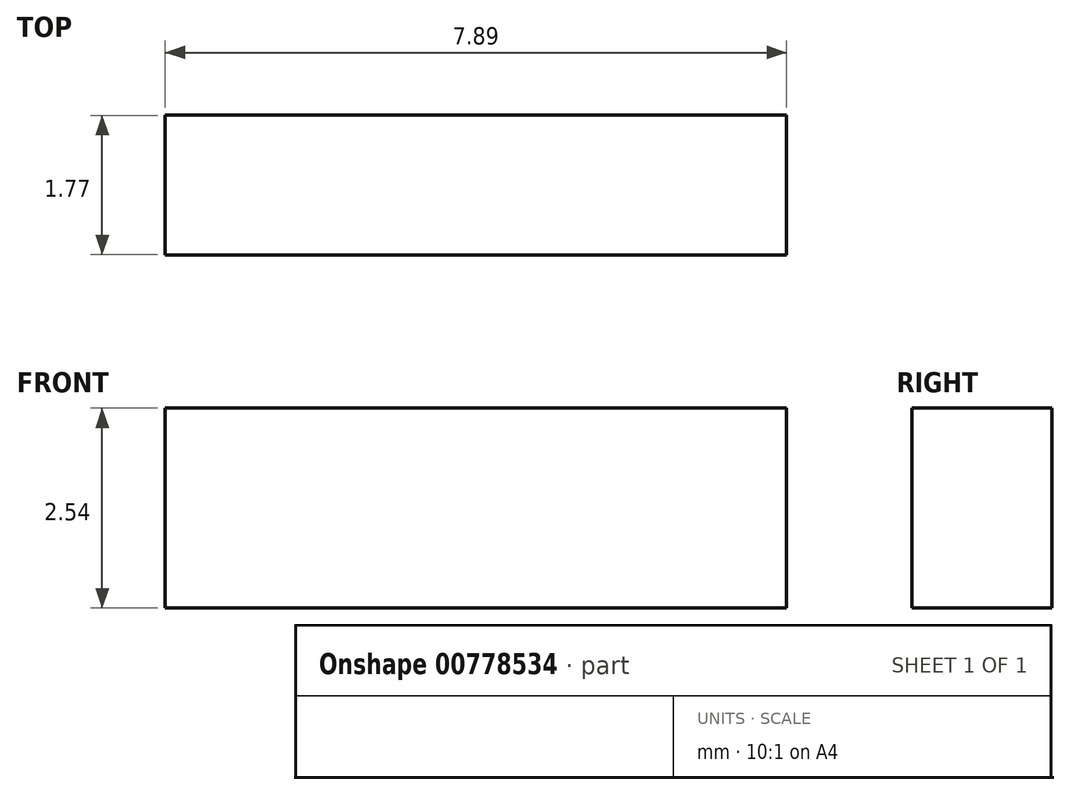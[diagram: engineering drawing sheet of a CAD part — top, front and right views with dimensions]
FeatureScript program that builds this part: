
annotation { "Feature Type Name" : "Feature", "Feature Type Description" : "" }
export const myFeature = defineFeature(function(context is Context, id is Id, definition is map)
    precondition{}
    {
        {
            var Q0;
            Q0=qCreatedBy(makeId("Front.planeOp"),FACE);
            var sketch = newSketch(context, id + "F0", { "sketchPlane" : qUnion([Q0])});
            skLineSegment(sketch, "E0.bottom", {"start": v(-12.97, 25.4) * mm, "end": v(11.1, 25.4) * mm});
            skLineSegment(sketch, "E0.top", {"start": v(-12.97, -20.32) * mm, "end": v(11.1, -20.32) * mm});
            skLineSegment(sketch, "E0.left", {"start": v(-12.97, 25.4) * mm, "end": v(-12.97, -20.32) * mm});
            skLineSegment(sketch, "E0.right", {"start": v(11.1, 25.4) * mm, "end": v(11.1, -20.32) * mm});
            skLineSegment(sketch, "E1", {"start": v(0, 9.9) * mm, "end": v(0, 4.81) * mm});
            skLineSegment(sketch, "E2", {"start": v(0, 4.81) * mm, "end": v(7.89, 4.81) * mm});
            skLineSegment(sketch, "E3", {"start": v(7.89, 4.81) * mm, "end": v(7.89, 9.9) * mm});
            skLineSegment(sketch, "E4", {"start": v(7.89, 9.9) * mm, "end": v(0, 9.9) * mm});
            skLineSegment(sketch, "E5", {"start": v(0, 7.35) * mm, "end": v(7.89, 7.35) * mm});
            skSolve(sketch);
        }
        {
            var Q0;
            Q0=makeQuery(id+"F0.imprint","IMPRINT",FACE,{"disambiguationData":[TD([[makeQuery(id+"F0.imprint","IMPRINT",EDGE,{"derivedFrom":sQuery(id+"F0.wireOp",EDGE,"E0.bottom")}),-1.0]])]});
            extrude(context, id + "F1", {"entities" : qUnion([Q0]), "depth" : 0.03 * mm, "offsetDistance" : 25.4 * mm});
        }
        {
            var Q0;
            Q0=makeQuery(id+"F1.opExtrude","CAP_FACE",FACE,{"disambiguationData":[OSD([sQuery(id+"F0.wireOp",EDGE,"E0.bottom"),sQuery(id+"F0.wireOp",EDGE,"E0.top"),sQuery(id+"F0.wireOp",EDGE,"E0.left"),sQuery(id+"F0.wireOp",EDGE,"E0.right"),sQuery(id+"F0.wireOp",EDGE,"E1"),sQuery(id+"F0.wireOp",EDGE,"E2"),sQuery(id+"F0.wireOp",EDGE,"E3"),sQuery(id+"F0.wireOp",EDGE,"E4")])],"isStart":false});
            var sketch = newSketch(context, id + "F2", { "sketchPlane" : qUnion([Q0])});
            skLineSegment(sketch, "E6", {"start": v(0, 9.9) * mm, "end": v(7.89, 9.9) * mm});
            skLineSegment(sketch, "E7", {"start": v(7.89, 9.9) * mm, "end": v(7.89, 7.35) * mm});
            skLineSegment(sketch, "E8", {"start": v(7.89, 7.35) * mm, "end": v(0, 7.35) * mm});
            skLineSegment(sketch, "E9", {"start": v(0, 7.35) * mm, "end": v(0, 9.9) * mm});
            skSolve(sketch);
        }
        {
            var Q0;
            Q0 = qSketchRegion(id + "F2", true);
            extrude(context, id + "F3", {"entities" : qUnion([Q0]), "depth" : 1.78 * mm, "offsetDistance" : 25.4 * mm});
        }
        {
            var Q0;
            Q0=makeQuery(id+"F1.opExtrude","CAP_FACE",FACE,{"disambiguationData":[OSD([sQuery(id+"F0.wireOp",EDGE,"E0.bottom"),sQuery(id+"F0.wireOp",EDGE,"E0.top"),sQuery(id+"F0.wireOp",EDGE,"E0.left"),sQuery(id+"F0.wireOp",EDGE,"E0.right"),sQuery(id+"F0.wireOp",EDGE,"E1"),sQuery(id+"F0.wireOp",EDGE,"E2"),sQuery(id+"F0.wireOp",EDGE,"E3"),sQuery(id+"F0.wireOp",EDGE,"E4")])],"isStart":false});
            var sketch = newSketch(context, id + "F4", { "sketchPlane" : qUnion([Q0])});
            skLineSegment(sketch, "E10", {"start": v(0, 4.81) * mm, "end": v(7.89, 4.81) * mm});
            skLineSegment(sketch, "E11", {"start": v(7.89, 4.81) * mm, "end": v(7.89, 7.35) * mm});
            skLineSegment(sketch, "E12", {"start": v(7.89, 7.35) * mm, "end": v(0, 7.35) * mm});
            skLineSegment(sketch, "E13", {"start": v(0, 7.35) * mm, "end": v(0, 4.81) * mm});
            skSolve(sketch);
        }
        {
            var Q0;
            Q0 = qSketchRegion(id + "F4", true);
            extrude(context, id + "F5", {"entities" : qUnion([Q0]), "operationType" : NewBodyOperationType.ADD, "depth" : -0.25 * mm, "offsetDistance" : 25.4 * mm});
        }
        {
            var Q0;
            Q0=makeQuery(id+"F1.opExtrude","SWEPT_BODY",BODY,{"disambiguationData":[OSD([sQuery(id+"F0.wireOp",EDGE,"E0.bottom"),sQuery(id+"F0.wireOp",EDGE,"E0.top"),sQuery(id+"F0.wireOp",EDGE,"E0.left"),sQuery(id+"F0.wireOp",EDGE,"E0.right"),sQuery(id+"F0.wireOp",EDGE,"E1"),sQuery(id+"F0.wireOp",EDGE,"E2"),sQuery(id+"F0.wireOp",EDGE,"E3"),sQuery(id+"F0.wireOp",EDGE,"E4")])]});
            deleteBodies(context, id + "F6", {"entities" : qUnion([Q0])});
        }
    });
